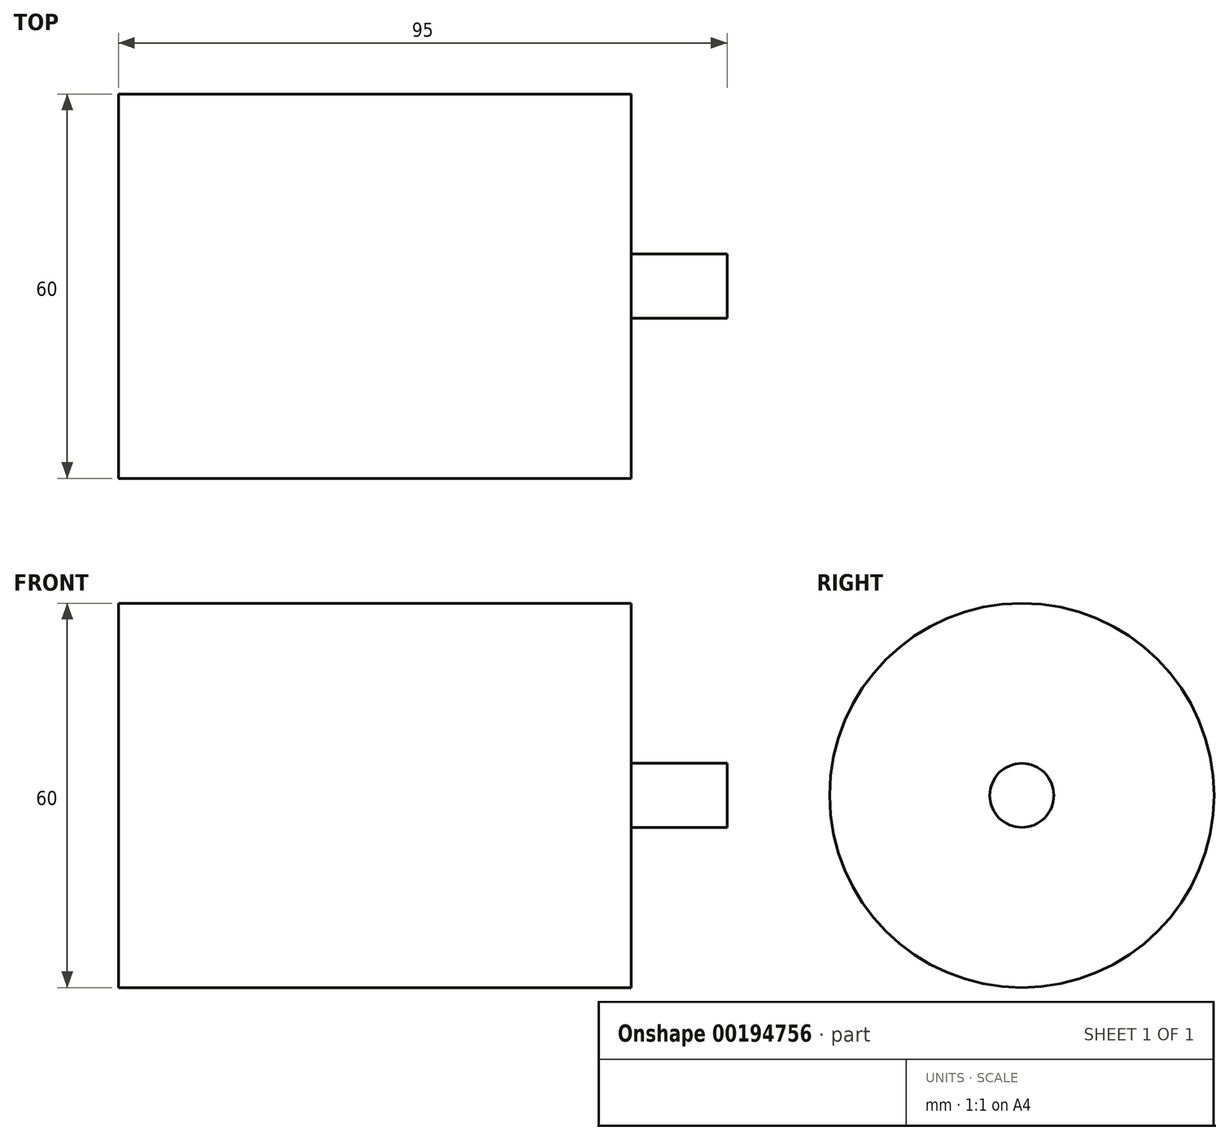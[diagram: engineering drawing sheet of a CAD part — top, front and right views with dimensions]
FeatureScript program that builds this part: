
annotation { "Feature Type Name" : "Feature", "Feature Type Description" : "" }
export const myFeature = defineFeature(function(context is Context, id is Id, definition is map)
    precondition{}
    {
        {
            var Q0;
            Q0=qCreatedBy(makeId("Front.planeOp"),FACE);
            var sketch = newSketch(context, id + "F0", { "sketchPlane" : qUnion([Q0])});
            skLineSegment(sketch, "E0", {"start": v(-63.55, 0) * mm, "end": v(-63.55, 30) * mm});
            skLineSegment(sketch, "E1", {"start": v(-63.55, 30) * mm, "end": v(16.45, 30) * mm});
            skLineSegment(sketch, "E2", {"start": v(16.45, 30) * mm, "end": v(16.45, 5) * mm});
            skLineSegment(sketch, "E3", {"start": v(16.45, 5) * mm, "end": v(31.45, 5) * mm});
            skLineSegment(sketch, "E4", {"start": v(31.45, 5) * mm, "end": v(31.45, 0) * mm});
            skLineSegment(sketch, "E5", {"start": v(31.45, 0) * mm, "end": v(-63.55, 0) * mm});
            skLineSegment(sketch, "E6", {"start": v(-71.96, 0) * mm, "end": v(56.87, 0) * mm, "construction": true});
            skSolve(sketch);
        }
        {
            var Q0;
            Q0=makeQuery(id+"F0.imprint","IMPRINT",FACE,{"disambiguationData":[TD([[makeQuery(id+"F0.imprint","IMPRINT",EDGE,{"derivedFrom":sQuery(id+"F0.wireOp",EDGE,"E0")}),-1.0]])]});
            var Q1;
            Q1=sQuery(id+"F0.wireOp",EDGE,"E6");
            revolve(context, id + "F1", {"entities" : qUnion([Q0]), "axis" : qUnion([Q1]), "revolveType" : RevolveType.FULL});
        }
    });
